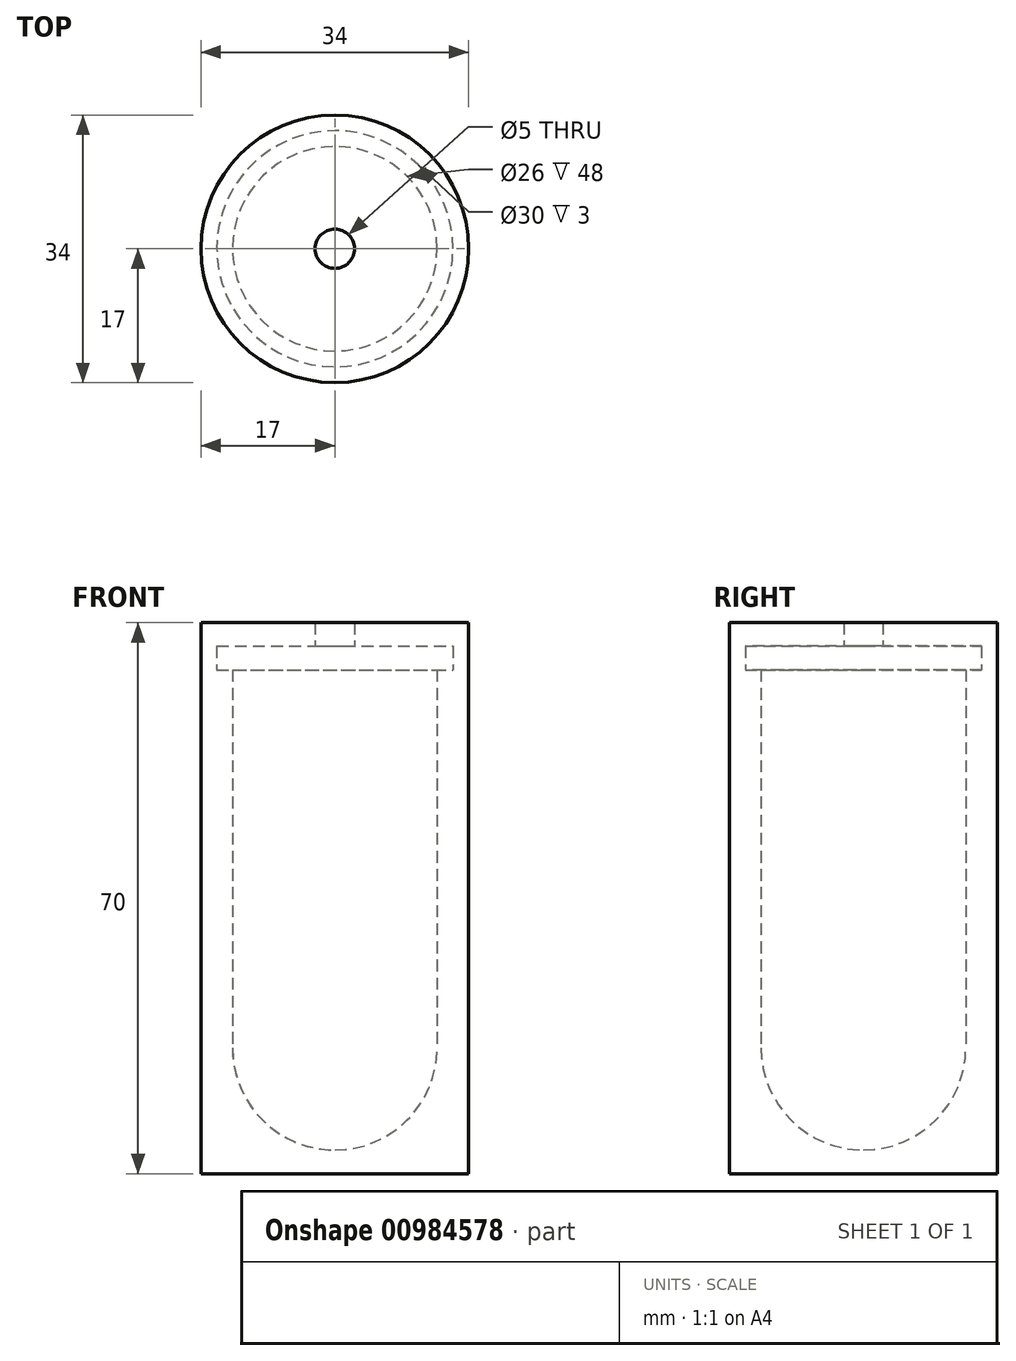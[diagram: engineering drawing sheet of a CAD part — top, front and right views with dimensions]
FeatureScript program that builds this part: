
annotation { "Feature Type Name" : "Feature", "Feature Type Description" : "" }
export const myFeature = defineFeature(function(context is Context, id is Id, definition is map)
    precondition{}
    {
        {
            var Q0;
            Q0=qCreatedBy(makeId("Front.planeOp"),FACE);
            var sketch = newSketch(context, id + "F0", { "sketchPlane" : qUnion([Q0])});
            skLineSegment(sketch, "E0.bottom", {"start": v(-13, 25.5) * mm, "end": v(13, 25.5) * mm});
            skLineSegment(sketch, "E0.top", {"start": v(-13, -25.5) * mm, "end": v(13, -25.5) * mm});
            skLineSegment(sketch, "E0.left", {"start": v(-13, 25.5) * mm, "end": v(-13, -25.5) * mm});
            skLineSegment(sketch, "E0.right", {"start": v(13, 25.5) * mm, "end": v(13, -25.5) * mm});
            skPoint(sketch, "E0.middle", {"position": v(0, 0) * mm});
            skLineSegment(sketch, "E1.bottom", {"start": v(-17, 28.5) * mm, "end": v(17, 28.5) * mm});
            skLineSegment(sketch, "E1.top", {"start": v(-17, -41.5) * mm, "end": v(17, -41.5) * mm});
            skLineSegment(sketch, "E1.left", {"start": v(-17, 28.5) * mm, "end": v(-17, -41.5) * mm});
            skLineSegment(sketch, "E1.right", {"start": v(17, 28.5) * mm, "end": v(17, -41.5) * mm});
            skLineSegment(sketch, "E2", {"start": v(0, -41.5) * mm, "end": v(0, -25.5) * mm});
            skLineSegment(sketch, "E3", {"start": v(0, 25.5) * mm, "end": v(0, 28.5) * mm, "construction": true});
            skLineSegment(sketch, "E4.bottom", {"start": v(15, 25.5) * mm, "end": v(-15, 25.5) * mm});
            skLineSegment(sketch, "E4.top", {"start": v(15, 22.5) * mm, "end": v(-15, 22.5) * mm});
            skLineSegment(sketch, "E4.left", {"start": v(15, 25.5) * mm, "end": v(15, 22.5) * mm});
            skLineSegment(sketch, "E4.right", {"start": v(-15, 25.5) * mm, "end": v(-15, 22.5) * mm});
            skPoint(sketch, "E4.middle", {"position": v(0, 24) * mm});
            skCircle(sketch, "E5", {"center": v(0, -25.5) * mm, "radius": 13 * mm});
            skLineSegment(sketch, "E6.bottom", {"start": v(-2.5, 28.5) * mm, "end": v(2.5, 28.5) * mm});
            skLineSegment(sketch, "E6.top", {"start": v(-2.5, 25.5) * mm, "end": v(2.5, 25.5) * mm});
            skLineSegment(sketch, "E6.left", {"start": v(-2.5, 28.5) * mm, "end": v(-2.5, 25.5) * mm});
            skLineSegment(sketch, "E6.right", {"start": v(2.5, 28.5) * mm, "end": v(2.5, 25.5) * mm});
            skPoint(sketch, "E6.middle", {"position": v(0, 27) * mm});
            skSolve(sketch);
        }
        {
            var Q0;
            {var subQ13=sQuery(id+"F0.wireOp",EDGE,"E1.left");Q0=makeQuery(id+"F0.imprint","IMPRINT",FACE,{"disambiguationData":[TD([[makeQuery(id+"F0.imprint","IMPRINT",EDGE,{"derivedFrom":subQ13}),1.0]])]});}
            var Q1;
            {var subQ0=sQuery(id+"F0.wireOp",EDGE,"hNINBkxJ-5WCb-KVtc-u2JZ-lkiryCvmdN34.left");Q1=makeQuery(id+"F0.imprint","IMPRINT",FACE,{"disambiguationData":[TD([[makeQuery(id+"F0.imprint","IMPRINT",EDGE,{"derivedFrom":subQ0}),1.0]])]});}
            var Q2;
            Q2=sQuery(id+"F0.wireOp",EDGE,"E2");
            revolve(context, id + "F1", {"surfaceOperationType" : NewSurfaceOperationType.NEW, "entities" : qUnion([Q0, Q1]), "axis" : qUnion([Q2]), "revolveType" : RevolveType.FULL});
        }
    });
